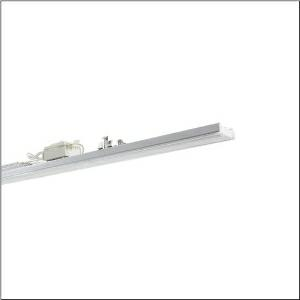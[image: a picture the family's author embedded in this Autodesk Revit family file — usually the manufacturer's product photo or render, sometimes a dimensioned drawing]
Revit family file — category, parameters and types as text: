
# Revit family: licross_21_recessed_mo_52tl12dn4axgd
name_source: partatom
category: Lighting Fixtures
units: mm (PartAtom-declared; Revit-internal decimal feet)

## family parameters
Cut with Voids When Loaded = No
Host = Face
Light Source = No
Part Type = Normal
Room Calculation Point = No
Round Connector Dimension = Use Diameter
Shared = No

## types (1)
- --- (1 x LED, 1540 lm, 9.7 W, 4000K)
    Apparent Load = 10 VA
    CIE Flux Codes = 72 92 99 100 100
    Color Rendering = 80
    Color Temperature = 4000K
    Default Elevation = 1800 mm
    Description = Licross 21 Recessed MO, luminaire insert, of sheet steel, galvanised, coil coated, white, length: 1.500mm, width: 66mm, height: 67mm, LED rated luminous flux: 10.280lm, light colour: 840, SDCM (Standard Deviation of Colour Matching)MacAdam ≤ 3 SDCM (initial), control gear: DALI 2 (for two DALI lines), with plug, 6-pole, with phase selection, mains connection: 220..240V, AC/DC, 0/50..60Hz, rated input power: 58W, without changeover relay, for emergency light function, for central battery installations according to EN 60598-2-22, internal wiring halogen-free, primary optical cover: cover, of PMMA, light emission: direct distribution, primary light characteristic: symmetric, protection rating (complete): IP40, insulation class (complete): insulation class I (protective earthing), certification: CE, ENEC, VDE, UKCA, protection symbol: D if used in an environment without relevant dust loads with corresponding accessories, impact resistance: IK06, permissible ambient temperature for indoor applications: -25..+35°C, standard: EN 60598-2-22, corresponds to IFS (International Featured Standards) requirements for safety and quality in the food industry, reducing of maximum allowable ambient temperature of 5°C with ceiling mounting, LABS conformity tested according to VDMA 24364:2018-05, The light source and the operating device comply with the requirements of the Ecodesign Regulation (EU) 2019/2020 and are replaceable in accordance with this regulation, packaging unit: 1 piece
    Height = 58 mm
    Lamp = 1 x LED
    Lamp Light Flux = 1540 lm
    Lamp Power = 9.7 W
    Lamp count = 1
    Length = 1500 mm
    Luminous efficacy = 159 lm/W
    Manufacturer = Siteco
    ModVariant = No
    Model = 52TL12DN4AXGD
    Mounting Place = Ceiling
    Mounting Type = Pendant
    Number of Poles = 1
    OnlyDefault = Yes
    Power Factor = 1
    Product Name = Licross 21 Recessed MO
    Product group = luminaire insert | ceiling pendant
    ProductGroupID = 901
    Protection Class = Protection class I
    Protection Degree = IP 40
    RLX_Detail_Level = 1
    RLX_Emergency_Light_Flux = 0 lm
    RLX_Emergency_Type = 0
    RLX_Emergency_Type_DB = No
    RlxData = <blob elided: 25413 chars, md5=70d835e1>
    Socket = socket
    Standby Power = 0 W
    System Light Flux = 1540 lm
    System Power = 10 W
    Type Comments = : DC mode (central or group accumulator) initial emergency light level
    Type Image = l_1296930.jpg
    URL = http://relux.com
    VarID = @adj_113231
    Voltage = 0 V
    Weight = 0.00 kg
    Width = 66 mm

## geometry (parser evidence)
native form markers: Blend x4, Sweep x11
no freeform markers — native parametric forms only
